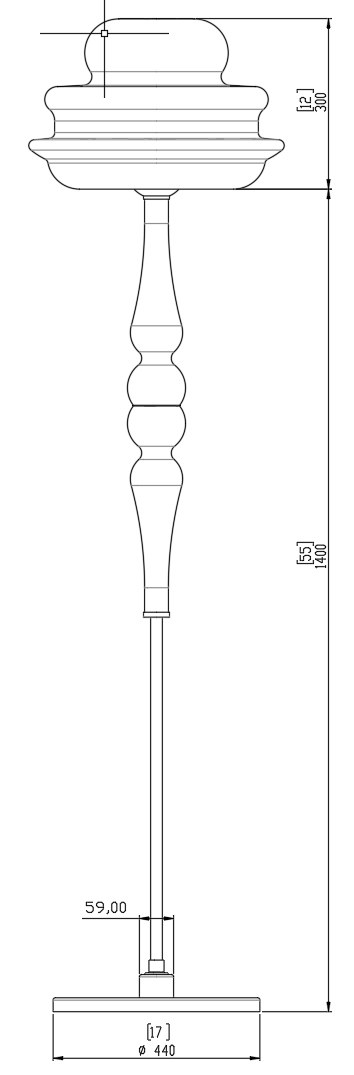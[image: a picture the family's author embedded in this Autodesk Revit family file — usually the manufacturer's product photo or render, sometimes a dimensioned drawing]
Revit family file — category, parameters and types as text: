
# Revit family: PEGGY SP 9-Suspension
name_source: partatom
category: Lighting Fixtures
units: mm (PartAtom-declared; Revit-internal decimal feet)

## family parameters
Always vertical = Yes
Cut with Voids When Loaded = No
Host = Ceiling
Light Source = No
OmniClass Number = 23.80.70.11
OmniClass Title = Luminaries for Internal Lighting
Part Type = Normal
Room Calculation Point = No
Round Connector Dimension = Use Diameter
Shared = No

## types (1)
- PEGGY SP 9
    Bulb Diametr = 15 mm  [stored 0.0492126 ft]
    Country = Europe
    Default Elevation = 0 mm  [stored 0 ft]
    Depth = 67 mm
    Description = SUSPENSION
    Designer = Hangar Design Group
    Manufacturer = Vistosi
    Manufacturer country = Italy
    Model = PEGGY
    Type Comments = Hangar Design Group
    URL = https://vistosi.com
    URL Product Page = https://vistosi.it
    Width = 180 mm

note: [stored X ft] marks values corroborated as IEEE doubles in the binary element streams (Revit-internal decimal feet)

## geometry (parser evidence)
native form markers: Sweep x7
no freeform markers — native parametric forms only
